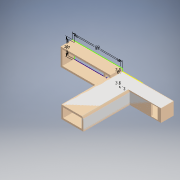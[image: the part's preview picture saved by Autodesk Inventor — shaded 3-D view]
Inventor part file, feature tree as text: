
AUTODESK INVENTOR PART (.ipt)
format: ipt  version: 2020 (Build 240168000, 168)  size: 445,440 bytes
history: native  units: mm
features: extrude x26, sketch x24, pattern_linear x3, other x2, chamfer x1
ambient origin geometry x8: Origin, YZ Plane, XZ Plane, XY Plane, X Axis, Y Axis, Z Axis, Center Point
bodies: Solid1 (feature_tree)
feature tree (56):
  extrude  "Extrusion1"  Depth=11.0mm
  extrude  "Extrusion2"  Depth=15.0mm
  sketch  "Sketch3"  dims[d4=70.0mm d5=0.0mm d7=1.0mm]
  extrude  "Extrusion3"  Depth=1.0mm
  sketch  "Sketch4"  dims[d8=1.0mm d9=6.0mm]
  extrude  "Extrusion4"  Depth=6.0mm
  extrude  "Extrusion5"  Depth=1.0mm
  extrude  "Extrusion6"  Depth=55.0mm
  extrude  "Extrusion7"  Depth=21.0mm
  extrude  "Extrusion8"  Depth=4.0mm
  extrude  "Extrusion9"  Depth=14.0mm TaperAngle=0.0deg
  extrude  "Extrusion10"  Depth=3.5mm
  extrude  "Extrusion11"  Depth=14.0mm TaperAngle=0.0deg
  extrude  "Extrusion12"  Depth=11.0mm
  extrude  "Extrusion13"  Depth=22.0mm TaperAngle=0.0deg
  extrude  "Extrusion14"  Depth=7.0mm
  extrude  "Extrusion15"  Depth=3.0mm
  extrude  "Extrusion16"  Depth=11.0mm TaperAngle=0.0deg
  extrude  "Extrusion17"  Depth=2.0mm
  extrude  "Extrusion18"  Depth=2.0mm
  extrude  "Extrusion19"  Depth=2.0mm TaperAngle=0.0deg
  extrude  "Extrusion20"  Depth=2.0mm
  extrude  "Extrusion21"  Depth=7.0mm TaperAngle=0.0deg
  extrude  "Extrusion22"  Depth=7.0mm TaperAngle=0.0deg
  extrude  "Extrusion23"  Depth=10.0mm
  pattern_linear  "Rectangular Pattern1"  Spacing1=2.0mm  [1 undecoded]
  pattern_linear  "Rectangular Pattern2"  Spacing1=2.0mm  [1 undecoded]
  extrude  "Extrusion24"  Depth=13.0mm
  pattern_linear  "Rectangular Pattern3"  Spacing1=2.0mm  [1 undecoded]
  extrude  "Extrusion25"  Depth=2.0mm TaperAngle=0.0deg
  extrude  "Extrusion27"  Depth=2.0mm TaperAngle=0.0deg
  chamfer  "Chamfer1"  Distance=5.0mm
  sketch  "Sketch1"  dims[d0=22.0mm d1=11.0mm]
  sketch  "Sketch2"  dims[d2=26.0mm d3=15.0mm]
  sketch  "Sketch5"  dims[d10=2.0mm d11=0.0mm d12=1.0mm]
  sketch  "Sketch6"  dims[d14=17.0mm d15=55.0mm]
  sketch  "Sketch7"  dims[d19=3.0mm d21=21.0mm]
  sketch  "Sketch8"  dims[d22=59.0mm d23=4.0mm]
  sketch  "Sketch9"  dims[d24=6.0mm d25=14.0mm d26=0.0mm]
  sketch  "Sketch10"  dims[d27=3.5mm d28=0.0mm d29=3.5mm]
  sketch  "Sketch11"  dims[d30=3.5mm d31=14.0mm d32=0.0mm]
  sketch  "Sketch12"  dims[d33=14.0mm d34=0.0mm d39=11.0mm]
  sketch  "Sketch13"  dims[d40=2.0mm d41=22.0mm d42=0.0mm]
  sketch  "Sketch14"  dims[d45=2.0mm d46=7.0mm]
  sketch  "Sketch15"  dims[d48=2.0mm d49=0.0mm d50=3.0mm]
  sketch  "Sketch16"  dims[d51=1.5mm d52=11.0mm d53=0.0mm]
  sketch  "Sketch17"  dims[d58=37.0mm d59=0.0mm d60=2.0mm]
  sketch  "Sketch18"  dims[d61=13.0mm d62=0.0mm d63=2.0mm]
  sketch  "Sketch19"  dims[d64=2.0mm d65=83.0mm d66=0.0mm]
  sketch  "Sketch20"  dims[d67=42.0mm d68=0.0mm d70=2.0mm]
  sketch  "Sketch21"  dims[d71=15.0mm d72=0.0mm d73=7.0mm d74=0.0mm]
  sketch  "Sketch22"  dims[d75=2.0mm d76=7.0mm d77=0.0mm]
  sketch  "Sketch23"  dims[d78=5.0mm d79=0.0mm d80=10.0mm]
  sketch  "Sketch25"  dims[d81=10.0mm d82=2.0mm d83=0.0mm d84=2.0mm d85=13.0mm d86=2.0mm d87=0.0mm d88=2.0mm d89=0.0mm d90=2.0mm d91=0.0mm d92=5.0mm d93=0.0mm d96=2.4mm d97=2.0mm d98=0.0mm d99=20.0mm d101=30.0mm d102=30.0mm d104=25.0mm d107=2.4mm d108=2.0mm d109=0.0mm d110=20.0mm d112=20.0mm d113=30.0mm d115=30.0mm d116=35.0mm d117=0.0mm d120=25.0mm d121=0.0mm d122=2.0mm d123=2.0mm d124=45.0deg d35=0.5mm d36=0.872665mm d69=0.5mm]
  other  "Composite1"
  other  "Srf1"
note: 3 required parameter values undecoded (feature->parameter linkage not recoverable at this tier; creation-order binding heuristic only, values carry confidence <= 0.55)
